# Revit family: Magnuson-Message_Boards_Pantalla-
name_source: partatom
category: Furniture
revit_build: Autodesk Revit 2016 (Build: 20150220_1215(x64)
units: mm (PartAtom-declared; Revit-internal decimal feet)

## family parameters
Always vertical = Yes
Cut with Voids When Loaded = No
OmniClass Number = 23.40.20.00
OmniClass Title = General Furniture and Specialties
Room Calculation Point = No
Shared = No
Work Plane-Based = No

## types (1)
- PANTALLA-FLR
    Assembly Code = E2020200
    Base Finish = MG - Steel, Wrought
    Depth = 18 1/8"
    Description = Magnetic Vertical Panel Freestanding
    Glide Finish = MG - Black Plastic
    Height = 71 11/16"
    Keynote = 12500
    Low Emitting Finish = Yes
    Low Emitting Material = Yes
    Manufacturer = Magnuson Group
    Model = PANTALLA-FLR
    Panel Finish = MG - Steel, Wrought
    Percentage of Recycled Content = 0
    Revit File Built By = https://servex-us.com
    Salvage or Reuse = Yes
    Type Comments = Message Boards
    URL = www.magnusongroup.com
    Width = 17 3/4"

## geometry (parser evidence)
native form markers: Sweep x3
no freeform markers — native parametric forms only
